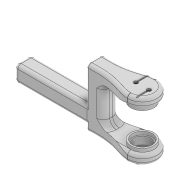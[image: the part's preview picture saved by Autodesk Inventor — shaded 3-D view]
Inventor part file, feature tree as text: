
AUTODESK INVENTOR PART (.ipt)
format: ipt  version: 2020 (Build 240168000, 168)  size: 1,104,896 bytes
history: native  units: mm
features: extrude x8, sketch x8, fillet x6, mirror x2, plane x1, projected_geometry x1
ambient origin geometry x8: Origin, YZ Plane, XZ Plane, XY Plane, X Axis, Y Axis, Z Axis, Center Point
bodies: Solid1 (feature_tree)
feature tree (26):
  extrude  "Extrusion1"  Depth=18.0mm
  extrude  "Extrusion2"  Depth=4.5mm
  extrude  "Extrusion3"  Depth=9.0mm
  extrude  "Extrusion4"  Depth=22.0mm
  extrude  "Extrusion5"  Depth=22.0mm
  extrude  "Extrusion6"  Depth=5.0mm
  plane  "Work Plane1"
  mirror  "Mirror1"
  extrude  "Extrusion7"  Depth=14.0mm
  fillet  "Fillet8"  Radius=3.0mm
  fillet  "Fillet9"  Radius=14.0mm
  fillet  "Fillet10"  Radius=16.0mm
  fillet  "Fillet11"  Radius=5.2mm
  extrude  "Extrusion9"  Depth=5.2mm
  mirror  "Mirror3"
  fillet  "Fillet12"  Radius=2.4mm
  fillet  "Fillet13"  Radius=7.0mm
  sketch  "Sketch1"  dims[d0=41.0mm d1=18.0mm]
  sketch  "Sketch3"  dims[d2=9.0mm d3=0.0mm d4=4.5mm]
  sketch  "Sketch4"  dims[d5=5.0mm d6=9.0mm]
  sketch  "Sketch5"  dims[d7=2.5mm d8=22.0mm]
  sketch  "Sketch6"  dims[d9=0.0mm d10=0.0mm d11=22.0mm]
  sketch  "Sketch7"  dims[d12=2.0mm d13=5.0mm]
  sketch  "Sketch8"  dims[d14=3.0mm d15=14.0mm d16=3.0mm d17=14.0mm d18=16.0mm d19=0.0mm d23=5.2mm]
  projected_geometry  "Projected Loop1"
  sketch  "Sketch11"  dims[d24=2.4mm d25=0.0mm d26=5.2mm d27=2.4mm d28=0.0mm d29=7.0mm d30=6.0mm d31=1.0mm d32=0.0mm d37=2.0mm d38=17.5mm d39=0.75mm d40=0.0mm d41=0.0mm d46=5.2mm d47=2.0mm d48=2.0mm d49=1.0mm d50=1.0mm d51=1.0mm d52=0.2mm d54=0.24mm d55=0.0mm d56=0.5mm d57=0.5mm]
